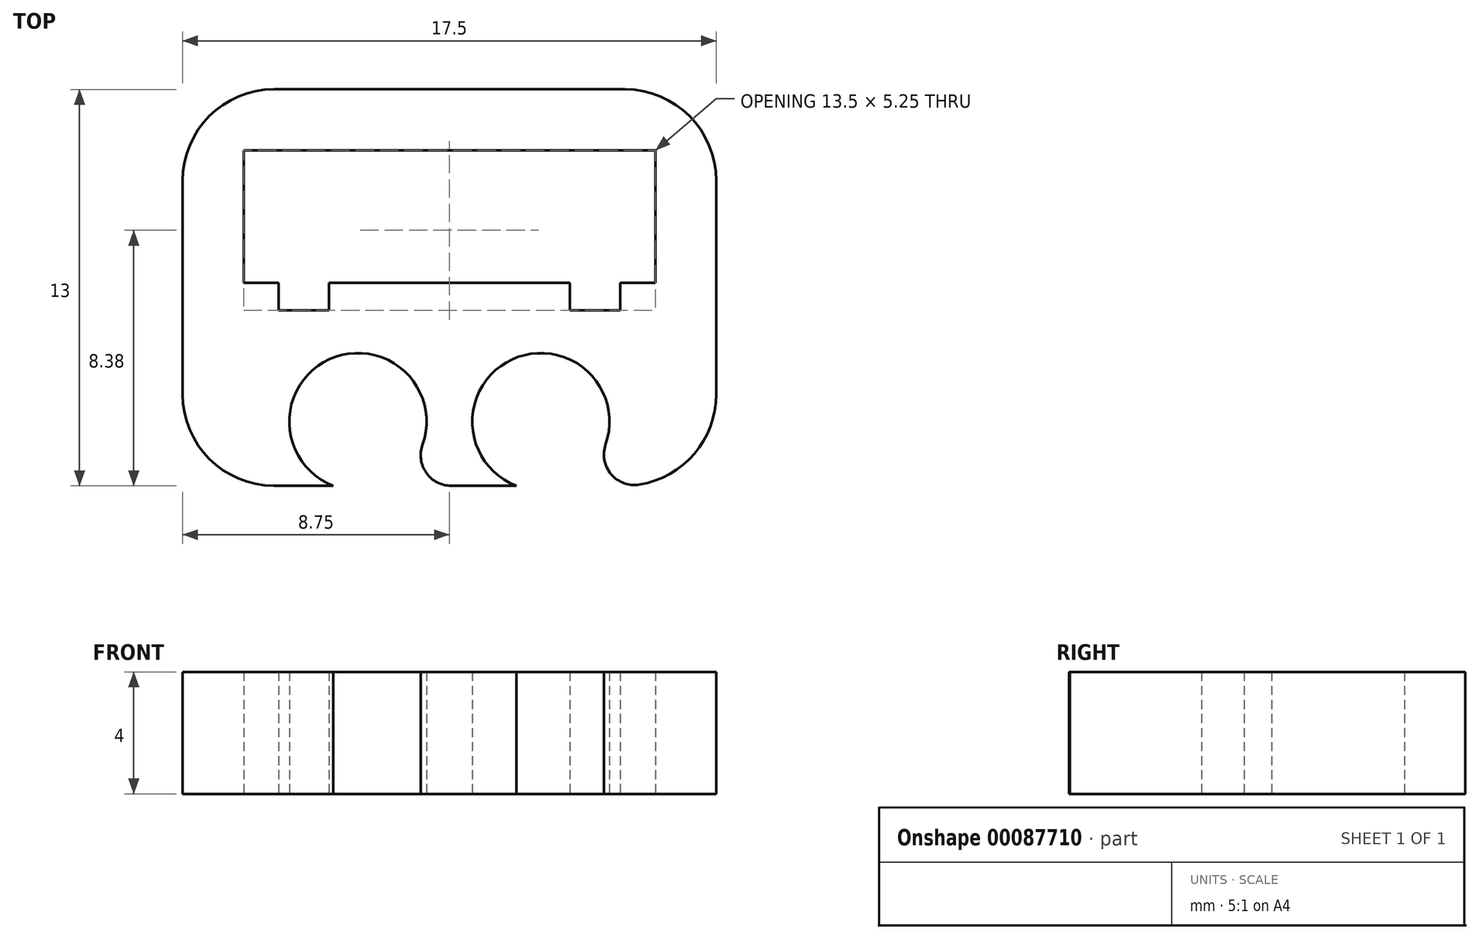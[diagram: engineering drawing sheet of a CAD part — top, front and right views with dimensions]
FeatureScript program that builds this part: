
annotation { "Feature Type Name" : "Feature", "Feature Type Description" : "" }
export const myFeature = defineFeature(function(context is Context, id is Id, definition is map)
    precondition{}
    {
        {
            var Q0;
            Q0=qCreatedBy(makeId("Top.planeOp"),FACE);
            var sketch = newSketch(context, id + "F0", { "sketchPlane" : qUnion([Q0])});
            skLineSegment(sketch, "E0.bottom", {"start": v(6.75, 2.17) * mm, "end": v(-6.75, 2.17) * mm});
            skLineSegment(sketch, "E0.top", {"start": v(6.75, -2.17) * mm, "end": v(-6.75, -2.17) * mm});
            skLineSegment(sketch, "E0.left", {"start": v(6.75, 2.17) * mm, "end": v(6.75, -2.17) * mm});
            skLineSegment(sketch, "E0.right", {"start": v(-6.75, 2.17) * mm, "end": v(-6.75, -2.17) * mm});
            skPoint(sketch, "E0.middle", {"position": v(0, 0) * mm});
            skLineSegment(sketch, "E1.top", {"start": v(-5.6, -3.08) * mm, "end": v(-3.95, -3.08) * mm});
            skLineSegment(sketch, "E1.left", {"start": v(-5.6, -2.17) * mm, "end": v(-5.6, -3.08) * mm});
            skLineSegment(sketch, "E1.right", {"start": v(-3.95, -2.17) * mm, "end": v(-3.95, -3.08) * mm});
            skLineSegment(sketch, "E2.MirrorCS", {"start": v(3.95, -2.17) * mm, "end": v(3.95, -3.08) * mm});
            skLineSegment(sketch, "E3.MirrorCS", {"start": v(5.6, -3.08) * mm, "end": v(3.95, -3.08) * mm});
            skLineSegment(sketch, "E4.MirrorCS", {"start": v(5.6, -2.17) * mm, "end": v(5.6, -3.08) * mm});
            skLineSegment(sketch, "E5.bottom", {"start": v(-8.75, 4.17) * mm, "end": v(8.75, 4.18) * mm});
            skLineSegment(sketch, "E5.top", {"start": v(-8.75, -8.83) * mm, "end": v(8.75, -8.82) * mm});
            skLineSegment(sketch, "E5.left", {"start": v(-8.75, 4.17) * mm, "end": v(-8.75, -8.83) * mm});
            skLineSegment(sketch, "E5.right", {"start": v(8.75, 4.18) * mm, "end": v(8.75, -8.82) * mm});
            skCircle(sketch, "E6", {"center": v(-3, -6.73) * mm, "radius": 2.25 * mm});
            skCircle(sketch, "E7", {"center": v(3, -6.73) * mm, "radius": 2.25 * mm});
            skSolve(sketch);
        }
        {
            var Q0;
            Q0=makeQuery(id+"F0.imprint","IMPRINT",FACE,{"disambiguationData":[TD([[makeQuery(id+"F0.imprint","IMPRINT",EDGE,{"derivedFrom":sQuery(id+"F0.wireOp",EDGE,"E0.bottom")}),-1.0]])]});
            extrude(context, id + "F1", {"entities" : qUnion([Q0]), "depth" : 4 * mm});
        }
        {
            var Q0;
            Q0=makeQuery(id+"F1.opExtrude","SWEPT_EDGE",EDGE,{"disambiguationData":[OSD([sQuery(id+"F0.wireOp",EDGE,"E5.bottom"),sQuery(id+"F0.wireOp",EDGE,"E5.left")])]});
            var Q1;
            Q1=makeQuery(id+"F1.opExtrude","SWEPT_EDGE",EDGE,{"disambiguationData":[OSD([sQuery(id+"F0.wireOp",EDGE,"E5.top"),sQuery(id+"F0.wireOp",EDGE,"E5.left")])]});
            var Q2;
            Q2=makeQuery(id+"F1.opExtrude","SWEPT_EDGE",EDGE,{"disambiguationData":[OSD([sQuery(id+"F0.wireOp",EDGE,"E5.top"),sQuery(id+"F0.wireOp",EDGE,"E5.right")])]});
            var Q3;
            Q3=makeQuery(id+"F1.opExtrude","SWEPT_EDGE",EDGE,{"disambiguationData":[OSD([sQuery(id+"F0.wireOp",EDGE,"E5.bottom"),sQuery(id+"F0.wireOp",EDGE,"E5.right")])]});
            fillet(context, id + "F2", {"entities" : qUnion([Q0, Q1, Q2, Q3]), "radius" : 3 * mm, "tangentPropagation" : true, "allowEdgeOverflow" : false});
        }
        {
            var Q0;
            {var subQ0=sQuery(id+"F0.wireOp",EDGE,"E7");var subQ1=sQuery(id+"F0.wireOp",EDGE,"E5.top");Q0=makeQuery(id+"F1.opExtrude","SWEPT_EDGE",EDGE,{"disambiguationData":[OSD([subQ1,subQ0]),TDD([makeQuery(id+"F0.imprint","INTERSECT",VERTEX,{"disambiguationData":[OD(0.0)],"derivedFrom":[subQ1,subQ0]})])]});}
            var Q1;
            {var subQ0=sQuery(id+"F0.wireOp",EDGE,"E6");var subQ1=sQuery(id+"F0.wireOp",EDGE,"E5.top");Q1=makeQuery(id+"F1.opExtrude","SWEPT_EDGE",EDGE,{"disambiguationData":[OSD([subQ1,subQ0]),TDD([makeQuery(id+"F0.imprint","INTERSECT",VERTEX,{"disambiguationData":[OD(1.0)],"derivedFrom":[subQ1,subQ0]})])]});}
            fillet(context, id + "F3", {"entities" : qUnion([Q0, Q1]), "radius" : 1 * mm, "tangentPropagation" : true, "allowEdgeOverflow" : false});
        }
    });
